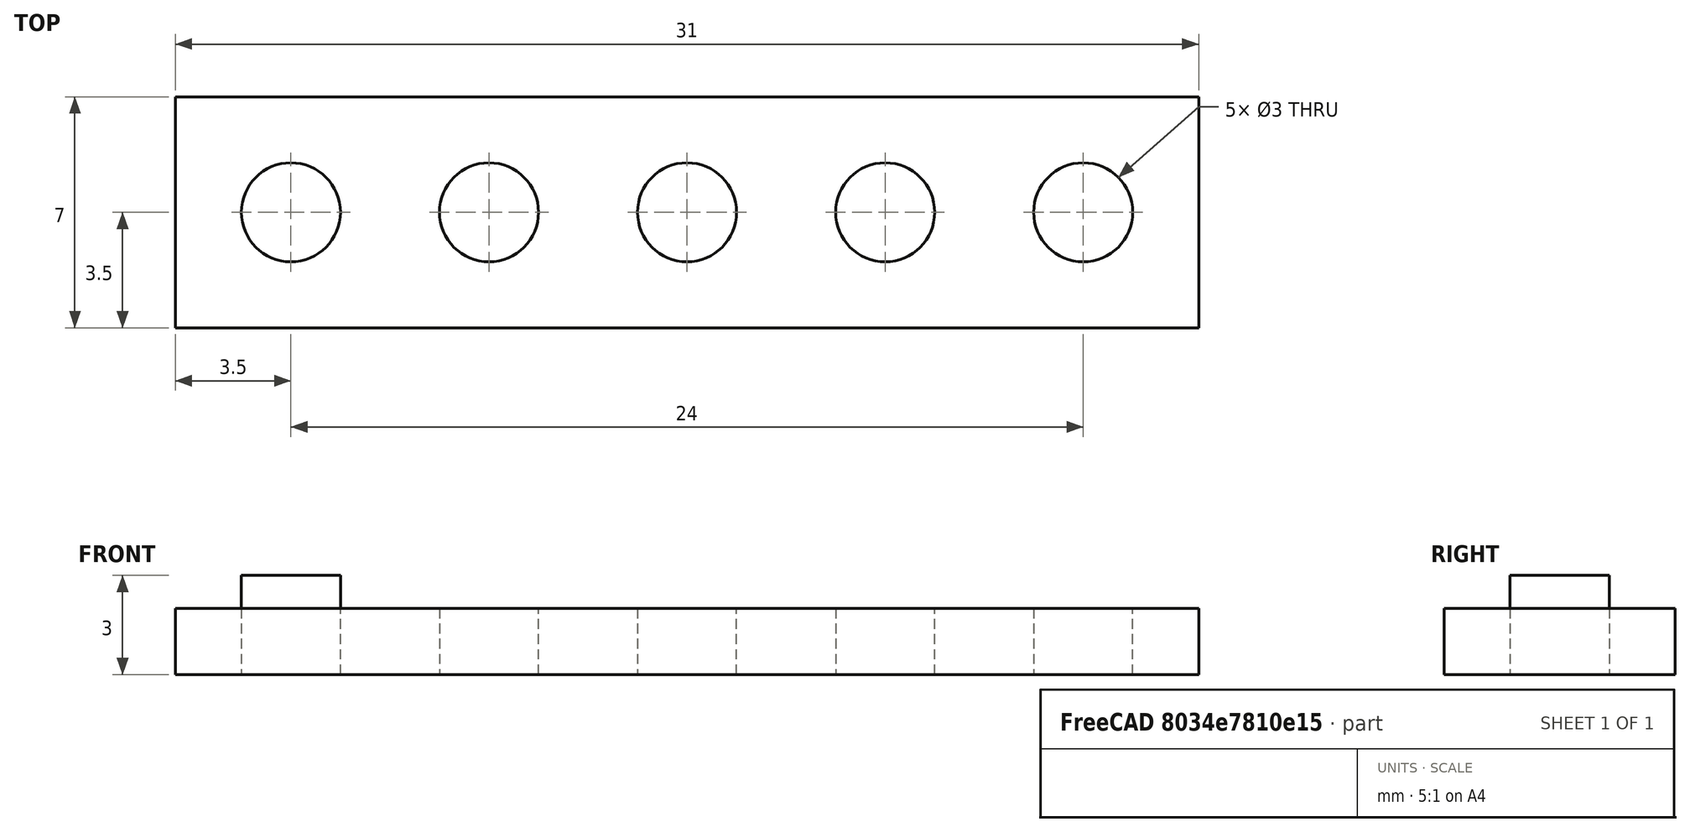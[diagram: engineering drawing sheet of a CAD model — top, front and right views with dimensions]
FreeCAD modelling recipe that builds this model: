
FCSTD DOCUMENT  (FreeCAD 1.0R39319 (Git))
Label: ojt1_t10r01_array_cylinder
License: All rights reserved
LicenseURL: https://en.wikipedia.org/wiki/All_rights_reserved
objects: Part::Box×1, Part::Cylinder×1, Part::FeaturePython×1, Part::Cut×1
note: 3 computed .brp shape members not serialized (recipe doc carries the construction recipe); baked Part::Feature solids carry a one-line shape summary decoded from their .brp

FEATURE [Part::Box] Box  label="Cub"
  AttacherType = Attacher::AttachEngine3D
  Height = 2
  Length = 31
  Width = 7
FEATURE [Part::Cylinder] Cylinder  label="Cilindre"
  Angle = 360
  AttacherType = Attacher::AttachEngine3D
  FirstAngle = 0
  Height = 3
  Placement = pos=(3.5,3.5,0) rot=(0,0,1;0rad)
  Radius = 1.5
  SecondAngle = 0
FEATURE [Part::FeaturePython] Array  # Draft array (typed FeaturePython)
  AlwaysSyncPlacement = false
  Angle = 360
  ArrayType = 0
  Axis = (0,0,1)
  Base = -> Cylinder
  Center = (0,0,0)
  Count = 5
  ExpandArray = false
  Fuse = false
  IntervalAxis = (0,0,0)
  IntervalX = (6,0,0)
  IntervalY = (0,0,0)
  IntervalZ = (0,0,100)
  NumberCircles = 3
  NumberPolar = 5
  NumberX = 5
  NumberY = 1
  NumberZ = 1
  PlacementList = 5 placements: arithmetic series from (3.5,3.5,0) step (6,0,0) to (27.5,3.5,0)
  RadialDistance = 50
  ScaleList = (5) [(1,1,1),(1,1,1),(1,1,1),(1,1,1),(1,1,1)]
  Symmetry = 1
  TangentialDistance = 25
FEATURE [Part::Cut] Cut
  Base = -> Box
  Refine = true
  Tool = -> Array
